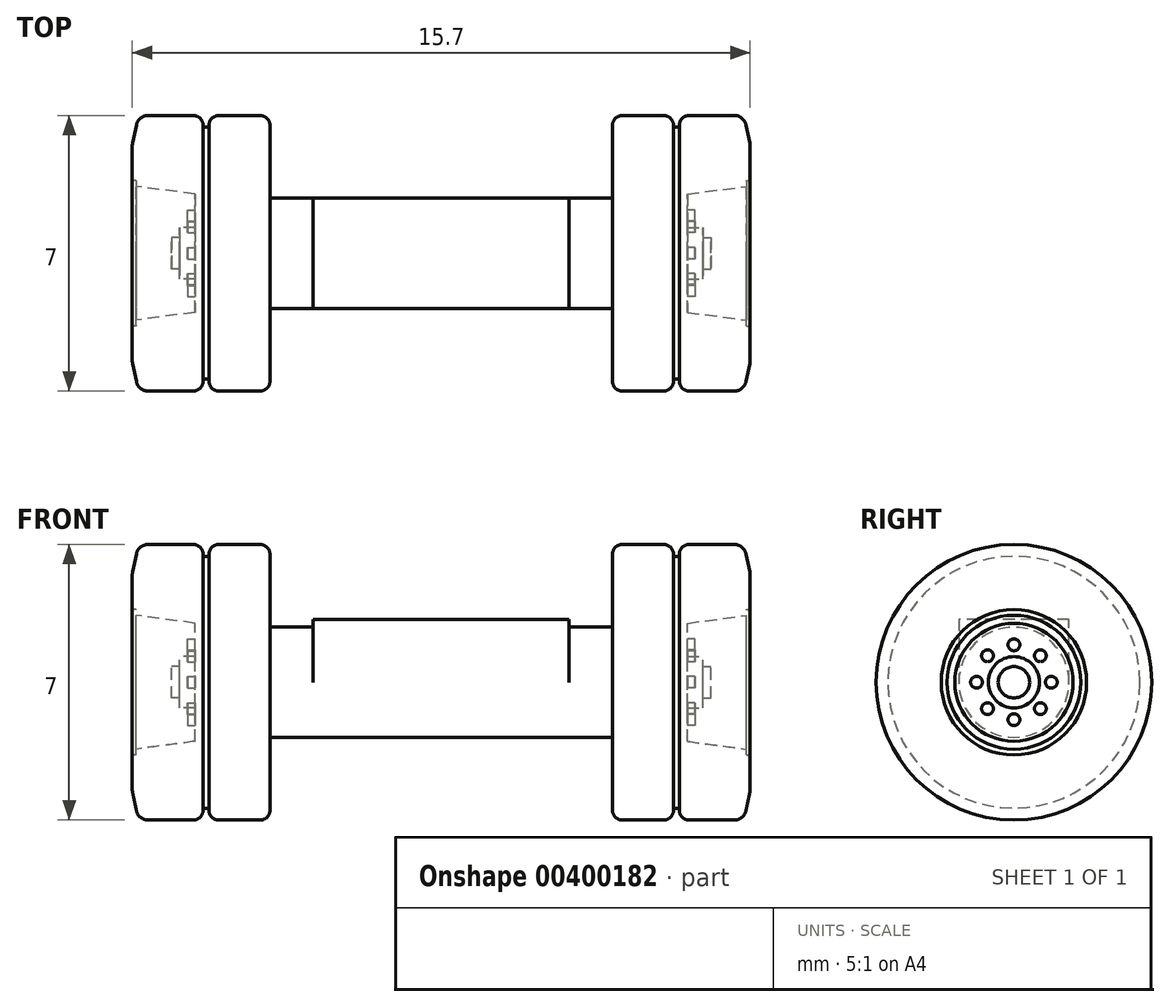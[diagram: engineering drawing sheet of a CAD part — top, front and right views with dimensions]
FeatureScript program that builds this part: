
annotation { "Feature Type Name" : "Feature", "Feature Type Description" : "" }
export const myFeature = defineFeature(function(context is Context, id is Id, definition is map)
    precondition{}
    {
        {
            var Q0;
            Q0=qCreatedBy(makeId("Front.planeOp"),FACE);
            var sketch = newSketch(context, id + "F0", { "sketchPlane" : qUnion([Q0])});
            skLineSegment(sketch, "E0", {"start": v(0, 0) * mm, "end": v(-36.36, 0) * mm, "construction": true});
            skLineSegment(sketch, "E1", {"start": v(0, 0) * mm, "end": v(0, 0.4) * mm});
            skLineSegment(sketch, "E2", {"start": v(0, 0.4) * mm, "end": v(-0.2, 0.4) * mm});
            skLineSegment(sketch, "E3", {"start": v(-0.2, 0.4) * mm, "end": v(-0.2, 0.65) * mm});
            skLineSegment(sketch, "E4", {"start": v(-0.2, 0.65) * mm, "end": v(-0.6, 0.65) * mm});
            skLineSegment(sketch, "E5", {"start": v(-0.6, 0.65) * mm, "end": v(-0.6, 1.5) * mm});
            skLineSegment(sketch, "E6", {"start": v(-0.6, 1.5) * mm, "end": v(0.9, 1.7) * mm});
            skLineSegment(sketch, "E7", {"start": v(1, 1.9) * mm, "end": v(1, 2.7) * mm});
            skLineSegment(sketch, "E8", {"start": v(0.6, 3.5) * mm, "end": v(-0.55, 3.5) * mm});
            skLineSegment(sketch, "E9", {"start": v(-0.8, 3.25) * mm, "end": v(-0.8, 3.2) * mm});
            skLineSegment(sketch, "E10", {"start": v(-0.8, 3.2) * mm, "end": v(-0.95, 3.2) * mm});
            skLineSegment(sketch, "E11", {"start": v(-0.95, 3.2) * mm, "end": v(-0.95, 3.25) * mm});
            skLineSegment(sketch, "E12", {"start": v(-1.2, 3.5) * mm, "end": v(-2.25, 3.5) * mm});
            skLineSegment(sketch, "E13", {"start": v(-2.5, 3.25) * mm, "end": v(-2.5, 1.4) * mm});
            skLineSegment(sketch, "E14", {"start": v(-3.6, 1.4) * mm, "end": v(-3.6, 0) * mm});
            skLineSegment(sketch, "E15", {"start": v(-3.6, 0) * mm, "end": v(0, 0) * mm});
            skLineSegment(sketch, "E16", {"start": v(0.9, 1.7) * mm, "end": v(0.9, 1.85) * mm});
            skLineSegment(sketch, "E17", {"start": v(0.9, 1.85) * mm, "end": v(0.95, 1.85) * mm});
            skLineSegment(sketch, "E18", {"start": v(-3.6, 1.4) * mm, "end": v(-2.5, 1.4) * mm});
            skPoint(sketch, "E19.visualSharp", {"position": v(1, 3.5) * mm});
            skPoint(sketch, "E20.visualSharp", {"position": v(-2.5, 3.5) * mm});
            skArc(sketch, "E20.filletArc", {"start": v(-2.25, 3.5) * mm, "mid": v(-2.43, 3.43) * mm, "end": v(-2.5, 3.25) * mm});
            skPoint(sketch, "E21.visualSharp", {"position": v(-0.8, 3.5) * mm});
            skArc(sketch, "E21.filletArc", {"start": v(-0.55, 3.5) * mm, "mid": v(-0.73, 3.43) * mm, "end": v(-0.8, 3.25) * mm});
            skPoint(sketch, "E22.visualSharp", {"position": v(-0.95, 3.5) * mm});
            skArc(sketch, "E22.filletArc", {"start": v(-0.95, 3.25) * mm, "mid": v(-1.02, 3.43) * mm, "end": v(-1.2, 3.5) * mm});
            skPoint(sketch, "E23.visualSharp", {"position": v(1, 1.85) * mm});
            skArc(sketch, "E23.filletArc", {"start": v(0.95, 1.85) * mm, "mid": v(0.99, 1.87) * mm, "end": v(1, 1.9) * mm});
            skLineSegment(sketch, "E24", {"start": v(0.9, 3.26) * mm, "end": v(0.99, 2.8) * mm});
            skPoint(sketch, "E25.visualSharp", {"position": v(1, 2.75) * mm});
            skArc(sketch, "E25.filletArc", {"start": v(1, 2.7) * mm, "mid": v(1, 2.75) * mm, "end": v(0.99, 2.8) * mm});
            skPoint(sketch, "E26.visualSharp", {"position": v(0.84, 3.5) * mm});
            skArc(sketch, "E26.filletArc", {"start": v(0.9, 3.26) * mm, "mid": v(0.79, 3.43) * mm, "end": v(0.6, 3.5) * mm});
            skSolve(sketch);
        }
        {
            var Q0;
            Q0=qSketchRegion(id+"F0",true);
            var Q1;
            Q1=sQuery(id+"F0.wireOp",EDGE,"E0");
            revolve(context, id + "F1", {"entities" : qUnion([Q0]), "axis" : qUnion([Q1]), "revolveType" : RevolveType.FULL});
        }
        {
            var Q0;
            Q0=makeQuery(id+"F1.opRevolve","SWEPT_FACE",FACE,{"disambiguationData":[OSD([sQuery(id+"F0.wireOp",EDGE,"E5")])]});
            var sketch = newSketch(context, id + "F2", { "sketchPlane" : qUnion([Q0])});
            skCircle(sketch, "E27", {"center": v(0, 0) * mm, "radius": 0.95 * mm, "construction": true});
            skCircle(sketch, "E28", {"center": v(0, 0.95) * mm, "radius": 0.15 * mm});
            skSolve(sketch);
        }
        {
            var Q0;
            Q0=qSketchRegion(id+"F2",true);
            extrude(context, id + "F3", {"entities" : qUnion([Q0]), "operationType" : NewBodyOperationType.ADD, "depth" : 0.2 * mm});
        }
        {
            var Q0;
            Q0=makeQuery(id+"F1.opRevolve","SWEPT_BODY",BODY,{"disambiguationData":[OSD([sQuery(id+"F0.wireOp",EDGE,"E1"),sQuery(id+"F0.wireOp",EDGE,"E2"),sQuery(id+"F0.wireOp",EDGE,"E3"),sQuery(id+"F0.wireOp",EDGE,"E4"),sQuery(id+"F0.wireOp",EDGE,"E5"),sQuery(id+"F0.wireOp",EDGE,"E6"),sQuery(id+"F0.wireOp",EDGE,"E7"),sQuery(id+"F0.wireOp",EDGE,"E8"),sQuery(id+"F0.wireOp",EDGE,"E9"),sQuery(id+"F0.wireOp",EDGE,"E10"),sQuery(id+"F0.wireOp",EDGE,"E11"),sQuery(id+"F0.wireOp",EDGE,"E12"),sQuery(id+"F0.wireOp",EDGE,"E13"),sQuery(id+"F0.wireOp",EDGE,"E14"),sQuery(id+"F0.wireOp",EDGE,"MRLpm4EO-d1Rz-y1Wd-tjo4-32WrfEVe7Kie"),sQuery(id+"F0.wireOp",EDGE,"1fY617z1-xQKE-QZae-sQAy-9TSEcJzTBgR6"),sQuery(id+"F0.wireOp",EDGE,"E15"),sQuery(id+"F0.wireOp",EDGE,"E16"),sQuery(id+"F0.wireOp",EDGE,"E17"),sQuery(id+"F0.wireOp",EDGE,"E18")])]});
            var Q1;
            Q1=makeQuery(id+"F1.opRevolve","SWEPT_FACE",FACE,{"disambiguationData":[OSD([sQuery(id+"F0.wireOp",EDGE,"E2")])]});
            circularPattern(context, id + "F4", {"operationType" : NewBodyOperationType.ADD, "entities" : qUnion([Q0]), "axis" : qUnion([Q1]), "angle" : 360 * degree, "instanceCount" : 8, "equalSpace" : true});
        }
        {
            var Q0;
            Q0=makeQuery(id+"F1.opRevolve","SWEPT_FACE",FACE,{"disambiguationData":[OSD([sQuery(id+"F0.wireOp",EDGE,"E14")])]});
            var sketch = newSketch(context, id + "F5", { "sketchPlane" : qUnion([Q0])});
            skArc(sketch, "E29.0", {"start": v(-1.4, 0) * mm, "mid": v(0, -1.4) * mm, "end": v(1.4, 0) * mm});
            skLineSegment(sketch, "E30", {"start": v(-1.4, 0) * mm, "end": v(-1.4, 1.6) * mm});
            skLineSegment(sketch, "E31", {"start": v(-1.4, 1.6) * mm, "end": v(1.4, 1.6) * mm});
            skLineSegment(sketch, "E32", {"start": v(1.4, 1.6) * mm, "end": v(1.4, 0) * mm});
            skSolve(sketch);
        }
        {
            var Q0;
            Q0=qSketchRegion(id+"F5",true);
            extrude(context, id + "F6", {"entities" : qUnion([Q0]), "operationType" : NewBodyOperationType.ADD, "depth" : 3.25 * mm});
        }
        {
            var Q0;
            Q0=makeQuery(id+"F1.opRevolve","SWEPT_BODY",BODY,{"disambiguationData":[OSD([sQuery(id+"F0.wireOp",EDGE,"E1"),sQuery(id+"F0.wireOp",EDGE,"E2"),sQuery(id+"F0.wireOp",EDGE,"E3"),sQuery(id+"F0.wireOp",EDGE,"E4"),sQuery(id+"F0.wireOp",EDGE,"E5"),sQuery(id+"F0.wireOp",EDGE,"E6"),sQuery(id+"F0.wireOp",EDGE,"E7"),sQuery(id+"F0.wireOp",EDGE,"E8"),sQuery(id+"F0.wireOp",EDGE,"E9"),sQuery(id+"F0.wireOp",EDGE,"E10"),sQuery(id+"F0.wireOp",EDGE,"E11"),sQuery(id+"F0.wireOp",EDGE,"E12"),sQuery(id+"F0.wireOp",EDGE,"E13"),sQuery(id+"F0.wireOp",EDGE,"E14"),sQuery(id+"F0.wireOp",EDGE,"E15"),sQuery(id+"F0.wireOp",EDGE,"E16"),sQuery(id+"F0.wireOp",EDGE,"E17"),sQuery(id+"F0.wireOp",EDGE,"E18"),sQuery(id+"F0.wireOp",EDGE,"E19.filletArc"),sQuery(id+"F0.wireOp",EDGE,"E20.filletArc"),sQuery(id+"F0.wireOp",EDGE,"E21.filletArc"),sQuery(id+"F0.wireOp",EDGE,"E22.filletArc"),sQuery(id+"F0.wireOp",EDGE,"E23.filletArc")])]});
            var Q1;
            Q1=makeQuery(id+"F6.opExtrude","CAP_FACE",FACE,{"disambiguationData":[OSD([sQuery(id+"F5.wireOp",EDGE,"E29.0"),sQuery(id+"F5.wireOp",EDGE,"E30"),sQuery(id+"F5.wireOp",EDGE,"E31"),sQuery(id+"F5.wireOp",EDGE,"E32")])],"isStart":false});
            mirror(context, id + "F7", {"operationType" : NewBodyOperationType.ADD, "entities" : qUnion([Q0]), "mirrorPlane" : qUnion([Q1])});
        }
    });
